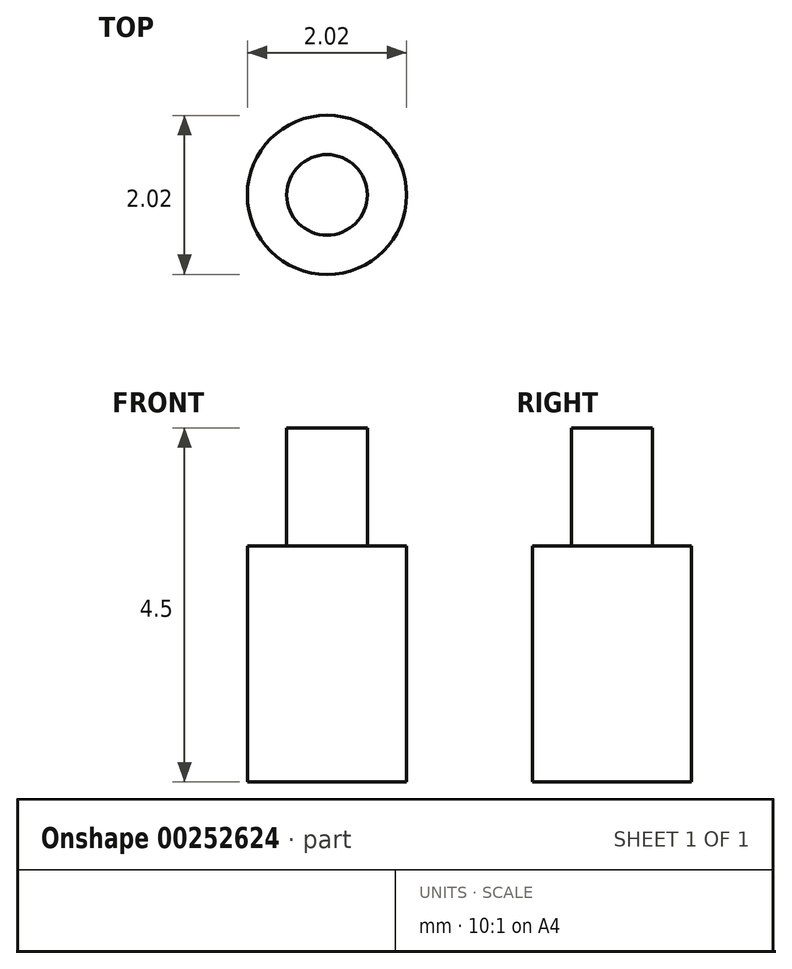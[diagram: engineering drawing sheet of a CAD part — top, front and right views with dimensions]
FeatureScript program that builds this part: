
annotation { "Feature Type Name" : "Feature", "Feature Type Description" : "" }
export const myFeature = defineFeature(function(context is Context, id is Id, definition is map)
    precondition{}
    {
        {
            var Q0;
            Q0=qCreatedBy(makeId("Front.planeOp"),FACE);
            var sketch = newSketch(context, id + "F0", { "sketchPlane" : qUnion([Q0])});
            skLineSegment(sketch, "E0.bottom", {"start": v(1.01, 1.5) * mm, "end": v(-1.01, 1.5) * mm});
            skLineSegment(sketch, "E0.top", {"start": v(1.01, -1.5) * mm, "end": v(-1.01, -1.5) * mm});
            skLineSegment(sketch, "E0.left", {"start": v(1.01, 1.5) * mm, "end": v(1.01, -1.5) * mm});
            skLineSegment(sketch, "E0.right", {"start": v(-1.01, 1.5) * mm, "end": v(-1.01, -1.5) * mm});
            skPoint(sketch, "E0.middle", {"position": v(0, 0) * mm});
            skLineSegment(sketch, "E1", {"start": v(0, 1.5) * mm, "end": v(0, -1.5) * mm});
            skSolve(sketch);
        }
        {
            var Q0;
            {var subQ0=sQuery(id+"F0.wireOp",EDGE,"E0.right");Q0=makeQuery(id+"F0.imprint","IMPRINT",FACE,{"disambiguationData":[TD([[makeQuery(id+"F0.imprint","IMPRINT",EDGE,{"derivedFrom":subQ0}),1.0]])]});}
            var Q1;
            Q1=sQuery(id+"F0.wireOp",EDGE,"E1");
            revolve(context, id + "F1", {"entities" : qUnion([Q0]), "axis" : qUnion([Q1]), "revolveType" : RevolveType.FULL});
        }
        {
            var Q0;
            Q0=makeQuery(id+"F1.opRevolve","SWEPT_FACE",FACE,{"disambiguationData":[OSD([sQuery(id+"F0.wireOp",EDGE,"E0.bottom")])]});
            shell(context, id + "F2", {"entities" : qUnion([Q0]), "thickness" : .5 * mm});
        }
        {
            var Q0;
            Q0=makeQuery(id+"F2.opShell","OFFSET_FACE",FACE,{"disambiguationData":[OSD([sQuery(id+"F0.wireOp",EDGE,"E0.top")])]});
            extrude(context, id + "F3", {"entities" : qUnion([Q0]), "operationType" : NewBodyOperationType.ADD, "depth" : 4 * mm});
        }
    });
